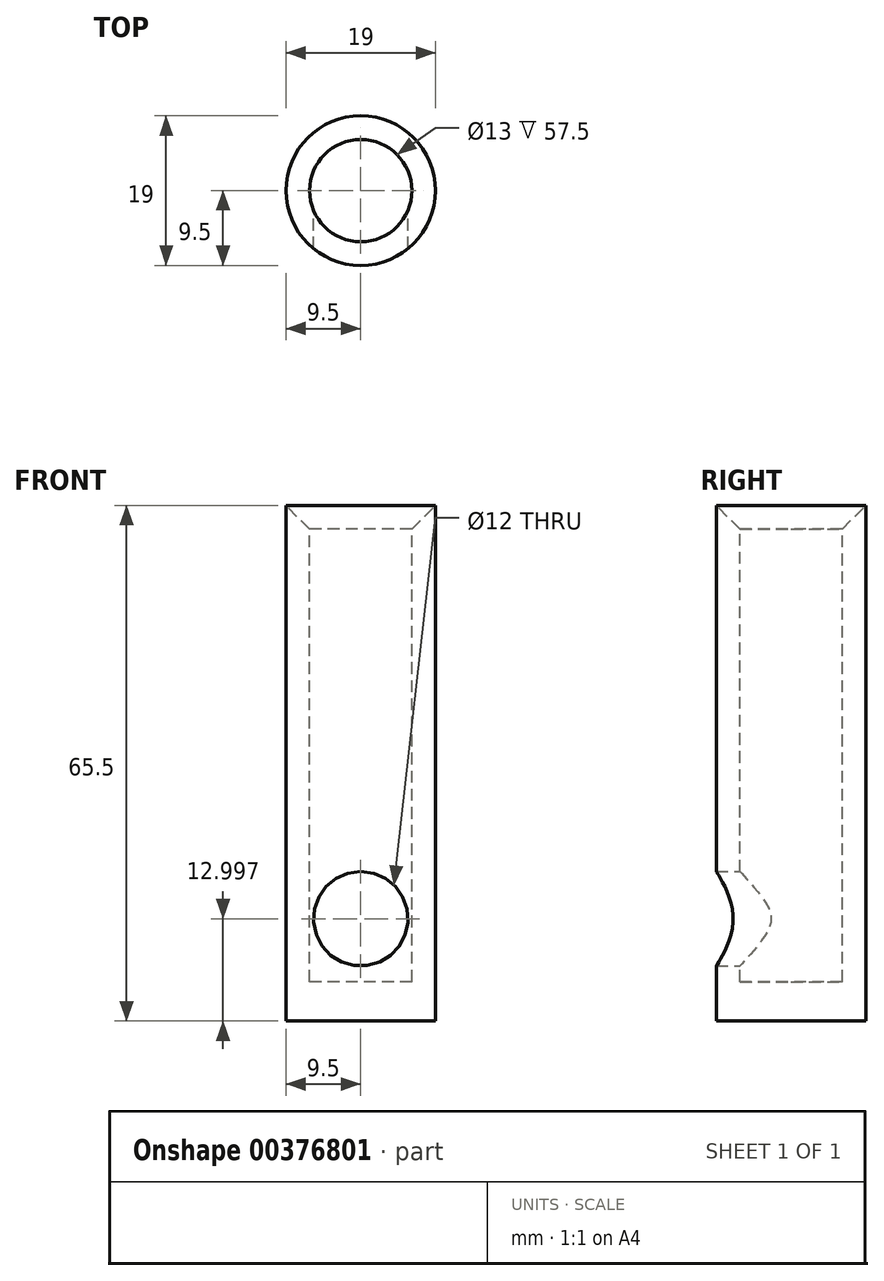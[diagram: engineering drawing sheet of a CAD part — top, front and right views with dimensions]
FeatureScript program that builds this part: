
annotation { "Feature Type Name" : "Feature", "Feature Type Description" : "" }
export const myFeature = defineFeature(function(context is Context, id is Id, definition is map)
    precondition{}
    {
        {
            var Q0;
            Q0=qCreatedBy(makeId("Front.planeOp"),FACE);
            var sketch = newSketch(context, id + "F0", { "sketchPlane" : qUnion([Q0])});
            skLineSegment(sketch, "E0", {"start": v(0, -24.9) * mm, "end": v(9.5, -24.9) * mm});
            skLineSegment(sketch, "E1", {"start": v(9.5, -24.9) * mm, "end": v(9.5, 40.6) * mm});
            skLineSegment(sketch, "E2", {"start": v(9.5, 40.6) * mm, "end": v(6.5, 37.6) * mm});
            skLineSegment(sketch, "E3", {"start": v(6.5, 37.6) * mm, "end": v(6.5, -19.9) * mm});
            skLineSegment(sketch, "E4", {"start": v(6.5, -19.9) * mm, "end": v(0, -19.9) * mm});
            skLineSegment(sketch, "E5", {"start": v(0, -19.9) * mm, "end": v(0, -24.9) * mm});
            skPoint(sketch, "E6", {"position": v(0, -11.9) * mm});
            skSolve(sketch);
        }
        {
            var Q0;
            Q0=makeQuery(id+"F0.imprint","IMPRINT",FACE,{"disambiguationData":[TD([[makeQuery(id+"F0.imprint","IMPRINT",EDGE,{"derivedFrom":sQuery(id+"F0.wireOp",EDGE,"E0")}),1.0]])]});
            var Q1;
            Q1=sQuery(id+"F0.wireOp",EDGE,"E5");
            revolve(context, id + "F1", {"entities" : qUnion([Q0]), "axis" : qUnion([Q1]), "revolveType" : RevolveType.FULL});
        }
        {
            var Q0;
            Q0=sQuery(id+"F0.wireOp",VERTEX,"E6");
            var Q1;
            Q1=makeQuery(id+"F1.opRevolve","SWEPT_BODY",BODY,{"disambiguationData":[OSD([sQuery(id+"F0.wireOp",EDGE,"E0"),sQuery(id+"F0.wireOp",EDGE,"E1"),sQuery(id+"F0.wireOp",EDGE,"E2"),sQuery(id+"F0.wireOp",EDGE,"E3"),sQuery(id+"F0.wireOp",EDGE,"E4"),sQuery(id+"F0.wireOp",EDGE,"E5")])]});
            hole(context, id + "F2", {"style" : HoleStyle.SIMPLE, "endStyle" : HoleEndStyle.THROUGH, "oppositeDirection" : true, "holeDiameter" : 12 * mm, "isTappedThrough" : true, "tappedDepth" : 12 * mm, "tapClearance" : 3, "startFromSketch" : true, "locations" : qUnion([Q0]), "scope" : qUnion([Q1])});
        }
    });
